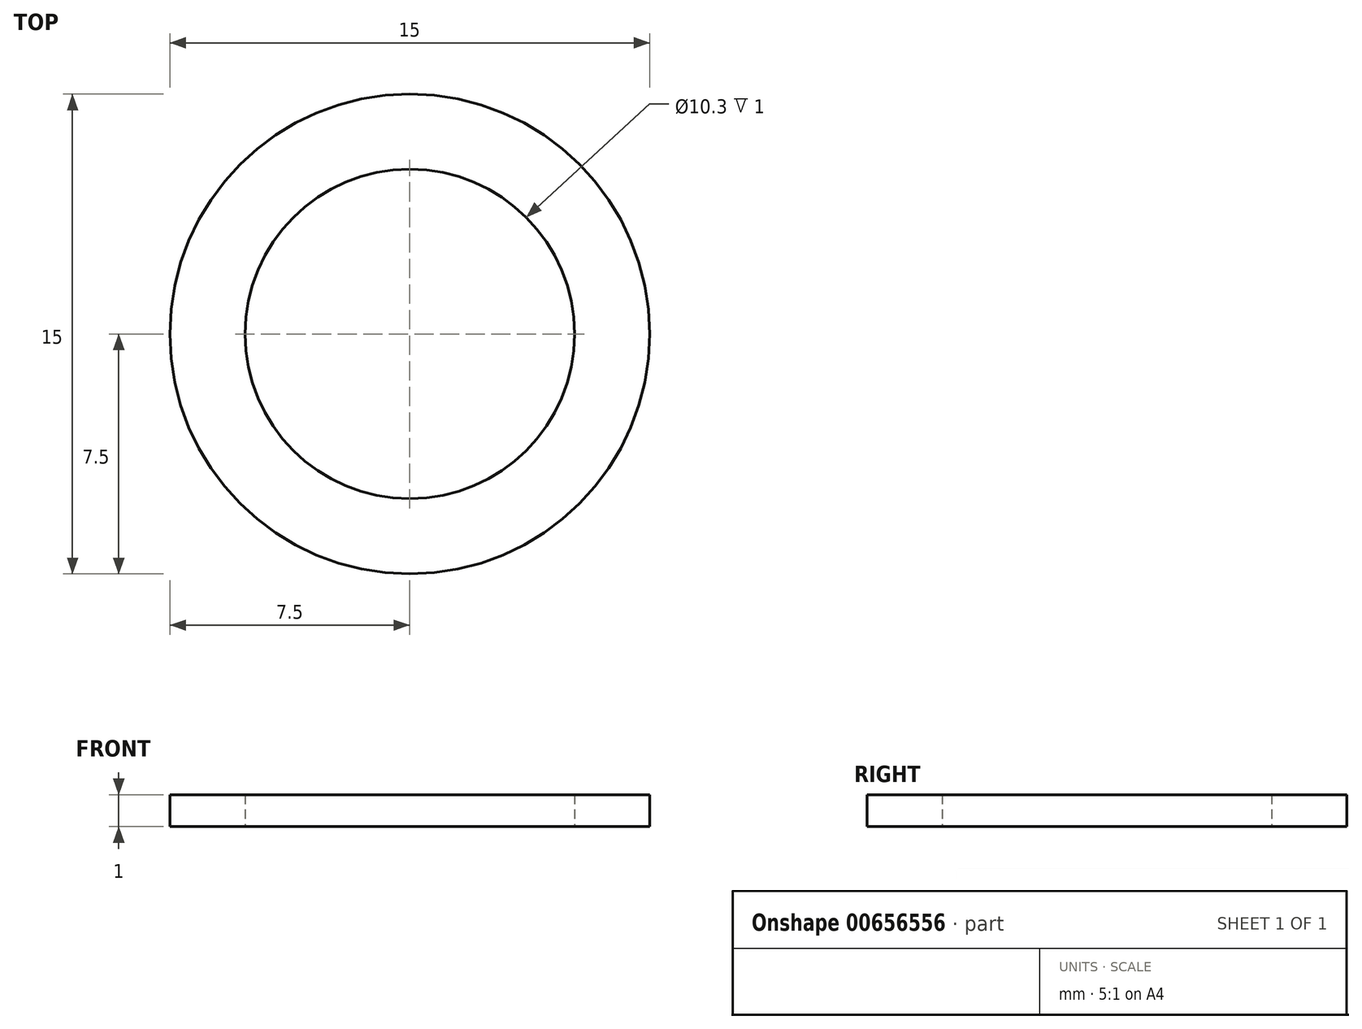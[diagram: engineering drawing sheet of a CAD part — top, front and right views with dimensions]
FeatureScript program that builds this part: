
annotation { "Feature Type Name" : "Feature", "Feature Type Description" : "" }
export const myFeature = defineFeature(function(context is Context, id is Id, definition is map)
    precondition{}
    {
        {
            var Q0;
            Q0=qCreatedBy(makeId("Top.planeOp"),FACE);
            var sketch = newSketch(context, id + "F0", { "sketchPlane" : qUnion([Q0])});
            skCircle(sketch, "E0", {"center": v(0, 0) * mm, "radius": 7.5 * mm});
            skCircle(sketch, "E1", {"center": v(0, 0) * mm, "radius": 5.15 * mm});
            skSolve(sketch);
        }
        {
            var Q0;
            Q0=makeQuery(id+"F0.imprint","IMPRINT",FACE,{"disambiguationData":[TD([[makeQuery(id+"F0.imprint","IMPRINT",EDGE,{"derivedFrom":sQuery(id+"F0.wireOp",EDGE,"E0")}),1.0]])]});
            extrude(context, id + "F1", {"entities" : qUnion([Q0]), "depth" : 1 * mm, "offsetDistance" : 25 * mm});
        }
    });
